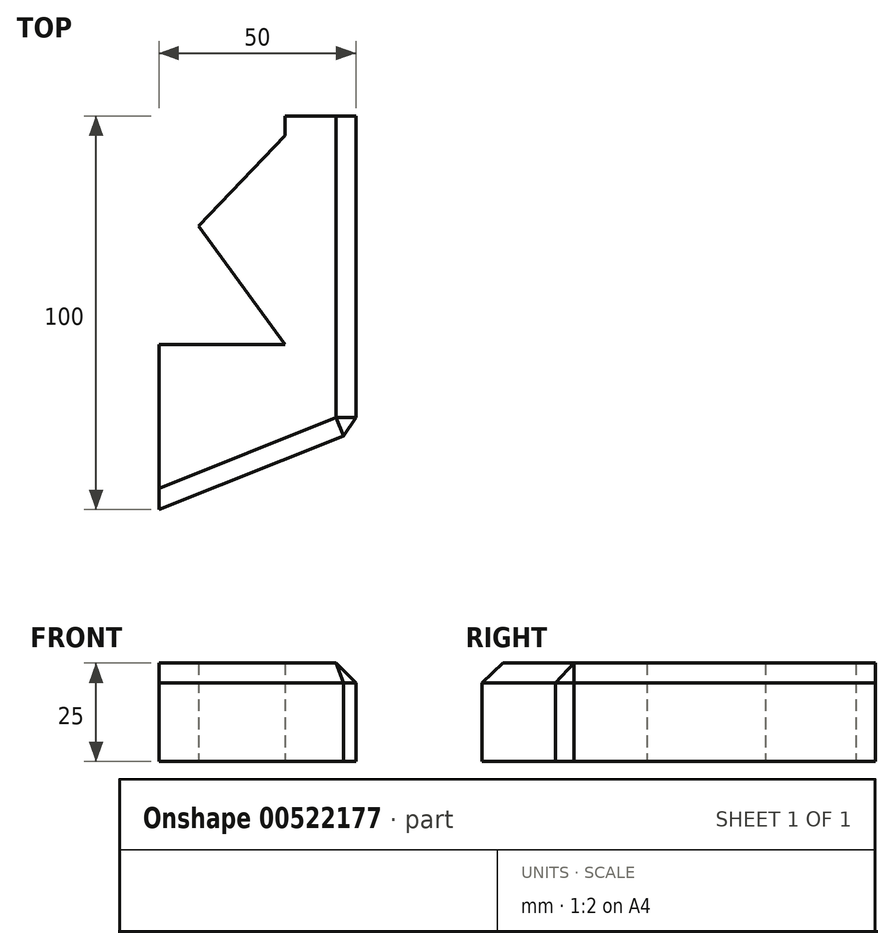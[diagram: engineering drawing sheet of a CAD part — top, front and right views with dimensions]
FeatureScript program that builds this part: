
annotation { "Feature Type Name" : "Feature", "Feature Type Description" : "" }
export const myFeature = defineFeature(function(context is Context, id is Id, definition is map)
    precondition{}
    {
        {
            var Q0;
            Q0=qCreatedBy(makeId("Top.planeOp"),FACE);
            var sketch = newSketch(context, id + "F0", { "sketchPlane" : qUnion([Q0])});
            skLineSegment(sketch, "E0", {"start": v(32, 53) * mm, "end": v(32, 58) * mm});
            skLineSegment(sketch, "E1", {"start": v(32, 58) * mm, "end": v(50, 58) * mm});
            skLineSegment(sketch, "E2", {"start": v(50, 58) * mm, "end": v(50, -22) * mm});
            skLineSegment(sketch, "E3", {"start": v(50, -22) * mm, "end": v(0, -42) * mm});
            skLineSegment(sketch, "E4", {"start": v(0, -42) * mm, "end": v(0, 0) * mm});
            skLineSegment(sketch, "E5", {"start": v(0, 0) * mm, "end": v(32, 0) * mm});
            skLineSegment(sketch, "E6", {"start": v(32, 0) * mm, "end": v(10, 30.06) * mm});
            skLineSegment(sketch, "E7", {"start": v(10, 30.06) * mm, "end": v(32, 53) * mm});
            skSolve(sketch);
        }
        {
            var Q0;
            Q0 = qSketchRegion(id + "F0", true);
            extrude(context, id + "F1", {"entities" : qUnion([Q0]), "depth" : 25 * mm, "offsetDistance" : 25 * mm});
        }
        {
            var Q0;
            Q0=makeQuery(id+"F1.opExtrude","CAP_EDGE",EDGE,{"disambiguationData":[OSD([sQuery(id+"F0.wireOp",EDGE,"E2")])],"isStart":false});
            var Q1;
            Q1=makeQuery(id+"F1.opExtrude","SWEPT_EDGE",EDGE,{"disambiguationData":[OSD([sQuery(id+"F0.wireOp",EDGE,"E2"),sQuery(id+"F0.wireOp",EDGE,"E3")])]});
            var Q2;
            Q2=makeQuery(id+"F1.opExtrude","CAP_EDGE",EDGE,{"disambiguationData":[OSD([sQuery(id+"F0.wireOp",EDGE,"E3")])],"isStart":false});
            chamfer(context, id + "F2", {"entities" : qUnion([Q0, Q1, Q2]), "width" : 5 * mm, "tangentPropagation" : true});
        }
    });
